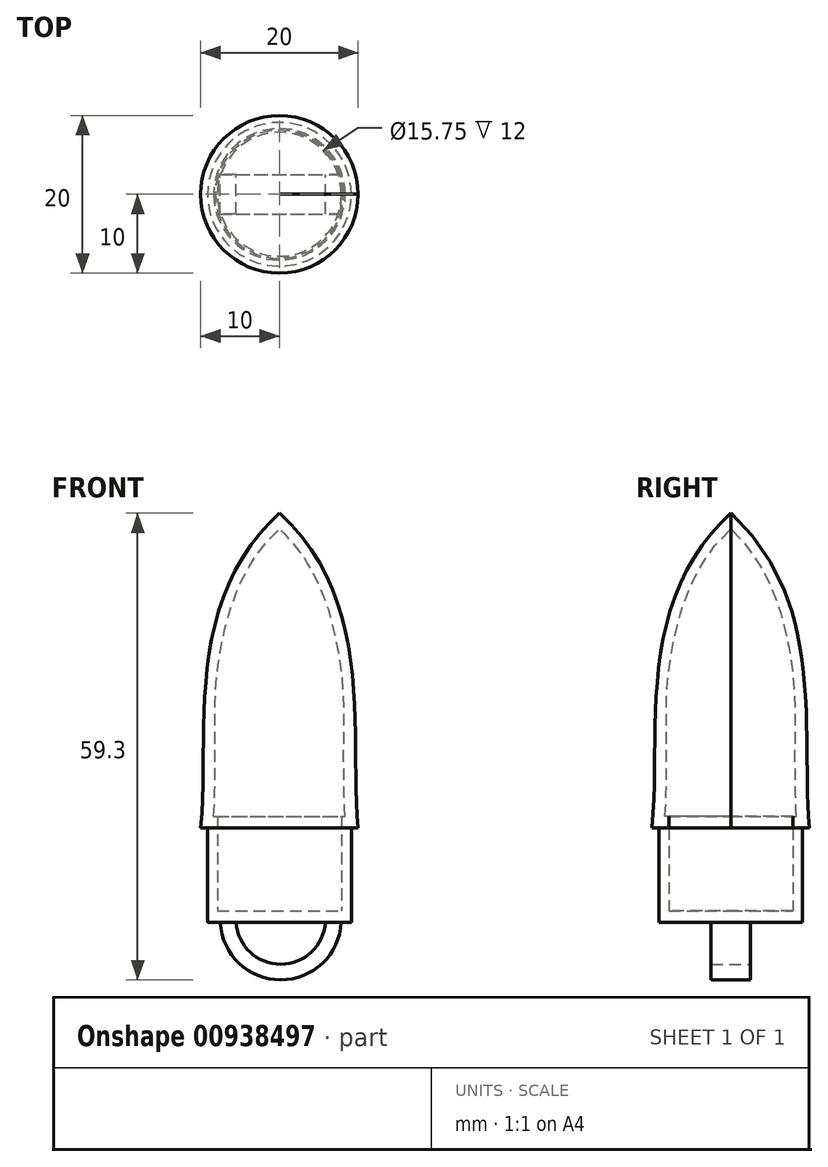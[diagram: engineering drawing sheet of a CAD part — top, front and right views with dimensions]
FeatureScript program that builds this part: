
annotation { "Feature Type Name" : "Feature", "Feature Type Description" : "" }
export const myFeature = defineFeature(function(context is Context, id is Id, definition is map)
    precondition{}
    {
        {
            var Q0;
            Q0=qCreatedBy(makeId("Front.planeOp"),FACE);
            var sketch = newSketch(context, id + "F0", { "sketchPlane" : qUnion([Q0])});
            skLineSegment(sketch, "E0", {"start": v(0, 0) * mm, "end": v(0, 40) * mm});
            skLineSegment(sketch, "E1", {"start": v(0, 0) * mm, "end": v(10, 0) * mm});
            skFitSpline(sketch, "E2", {"points": [v(10, 0) * mm, v(0, 40) * mm], "startDerivative": vector(-3.4, 36.26) * mm, "endDerivative": vector(-36.71, 33.56) * mm});
            skFitSpline(sketch, "E3.0", {"points": [v(8.5, -0.14) * mm, v(8.36, 1.42) * mm, v(8.22, 4.65) * mm, v(8.18, 11.43) * mm, v(8.04, 18.48) * mm, v(6.9, 25.3) * mm, v(5.34, 30.2) * mm, v(2.86, 34.77) * mm, v(0.44, 37.57) * mm, v(-1.01, 38.9) * mm]});
            skLineSegment(sketch, "E4.bottom", {"start": v(7.88, -12) * mm, "end": v(9.13, -12) * mm});
            skLineSegment(sketch, "E4.top", {"start": v(7.87, 1.5) * mm, "end": v(9.13, 1.5) * mm});
            skLineSegment(sketch, "E4.left", {"start": v(7.87, -12) * mm, "end": v(7.87, 1.5) * mm});
            skLineSegment(sketch, "E4.right", {"start": v(9.13, -12) * mm, "end": v(9.12, 1.5) * mm});
            skLineSegment(sketch, "E5.bottom", {"start": v(7.88, -12) * mm, "end": v(0, -12) * mm});
            skLineSegment(sketch, "E5.top", {"start": v(7.88, -10.5) * mm, "end": v(0, -10.5) * mm});
            skLineSegment(sketch, "E5.left", {"start": v(7.88, -12) * mm, "end": v(7.88, -10.5) * mm});
            skLineSegment(sketch, "E5.right", {"start": v(0, -12) * mm, "end": v(0, -10.5) * mm});
            skPoint(sketch, "E6.start.orphan", {"position": v(3.94, -14.5) * mm});
            skSolve(sketch);
        }
        {
            var Q0;
            {var subQ5=sQuery(id+"F0.wireOp",EDGE,"E2");Q0=makeQuery(id+"F0.imprint","IMPRINT",FACE,{"disambiguationData":[TD([[makeQuery(id+"F0.imprint","IMPRINT",EDGE,{"derivedFrom":subQ5}),1.0]])]});}
            var Q1;
            {var subQ1=sQuery(id+"F0.wireOp",EDGE,"E4.bottom");Q1=makeQuery(id+"F0.imprint","IMPRINT",FACE,{"disambiguationData":[TD([[makeQuery(id+"F0.imprint","IMPRINT",EDGE,{"derivedFrom":subQ1}),1.0]])]});}
            var Q2;
            {var subQ0=sQuery(id+"F0.wireOp",EDGE,"E3.0");var subQ1=sQuery(id+"F0.wireOp",EDGE,"E1");var subQ2=makeQuery(id+"F0.imprint","INTERSECT",VERTEX,{"derivedFrom":[subQ1,subQ0]});Q2=makeQuery(id+"F0.imprint","IMPRINT",FACE,{"disambiguationData":[TD([[makeQuery(id+"F0.imprint","IMPRINT",EDGE,{"disambiguationData":[TD([[subQ2,1.0]])],"derivedFrom":subQ1}),1.0]])]});}
            var Q3;
            {var subQ0=sQuery(id+"F0.wireOp",EDGE,"E3.0");var subQ1=sQuery(id+"F0.wireOp",EDGE,"E1");var subQ2=makeQuery(id+"F0.imprint","INTERSECT",VERTEX,{"derivedFrom":[subQ1,subQ0]});Q3=makeQuery(id+"F0.imprint","IMPRINT",FACE,{"disambiguationData":[TD([[makeQuery(id+"F0.imprint","IMPRINT",EDGE,{"disambiguationData":[TD([[subQ2,-1.0]])],"derivedFrom":subQ1}),1.0]])]});}
            var Q4;
            Q4=makeQuery(id+"F0.imprint","IMPRINT",FACE,{"disambiguationData":[TD([[makeQuery(id+"F0.imprint","IMPRINT",EDGE,{"derivedFrom":sQuery(id+"F0.wireOp",EDGE,"E5.bottom")}),-1.0]])]});
            var Q5;
            Q5=sQuery(id+"F0.wireOp",EDGE,"E0");
            revolve(context, id + "F1", {"surfaceOperationType" : NewSurfaceOperationType.NEW, "entities" : qUnion([Q0, Q1, Q2, Q3, Q4]), "axis" : qUnion([Q5]), "revolveType" : RevolveType.FULL});
        }
        {
            var Q0;
            Q0=qCreatedBy(makeId("Front.planeOp"),FACE);
            var sketch = newSketch(context, id + "F2", { "sketchPlane" : qUnion([Q0])});
            skArc(sketch, "E7", {"start": v(-7.52, -12) * mm, "mid": v(0.16, -19.3) * mm, "end": v(7.85, -12) * mm});
            skArc(sketch, "E8.0", {"start": v(-5.52, -11.9) * mm, "mid": v(0.16, -17.3) * mm, "end": v(5.85, -11.9) * mm});
            skLineSegment(sketch, "E9", {"start": v(7.85, -12) * mm, "end": v(-7.52, -12) * mm});
            skSolve(sketch);
        }
        {
            var Q0;
            {var subQ0=sQuery(id+"F2.wireOp",EDGE,"E7");Q0=makeQuery(id+"F2.imprint","IMPRINT",FACE,{"disambiguationData":[TD([[makeQuery(id+"F2.imprint","IMPRINT",EDGE,{"derivedFrom":subQ0}),1.0]])]});}
            extrude(context, id + "F3", {"entities" : qUnion([Q0]), "operationType" : NewBodyOperationType.ADD, "endBound" : BoundingType.SYMMETRIC, "depth" : 5 * mm, "offsetDistance" : 25 * mm});
        }
    });
